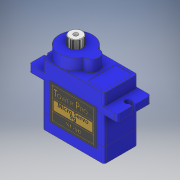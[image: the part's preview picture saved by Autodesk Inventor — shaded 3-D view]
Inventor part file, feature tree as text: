
AUTODESK INVENTOR PART (.ipt)
format: ipt  version: 2019 (Build 230136000, 136)  size: 1,554,432 bytes
history: native  units: in
note: dims shown in document units (in); Inventor stores cm internally (conversion verified against a paired STEP export)
features: other x13, plane x1, sketch x1
ambient origin geometry x8: Origin, YZ Plane, XZ Plane, XY Plane, X Axis, Y Axis, Z Axis, Center Point
bodies: Solid1 (feature_tree), Solid2 (feature_tree), Solid3 (feature_tree), Solid4 (feature_tree), Solid5 (feature_tree), Solid6 (feature_tree), Solid7 (feature_tree), Solid8 (feature_tree), Solid9 (feature_tree), Solid10 (feature_tree), Solid11 (feature_tree), Solid12 (feature_tree), Solid13 (feature_tree)
feature tree (15):
  plane  "Work Plane1"
  sketch  "Sketch1"  dims[d0=3.0in]
  other  "SG90 - Micro Servo 9g - Tower Pro.1-1-solid1"
  other  "SG90 - Micro Servo 9g - Tower Pro.1-1-solid2"
  other  "SG90 - Micro Servo 9g - Tower Pro.1-1-solid3"
  other  "SG90 - Micro Servo 9g - Tower Pro.1-1-solid4"
  other  "SG90 - Micro Servo 9g - Tower Pro.1-1-solid5"
  other  "SG90 - Micro Servo 9g - Tower Pro.1-1-solid6"
  other  "SG90 - Micro Servo 9g - Tower Pro.1-1-solid7"
  other  "SG90 - Micro Servo 9g - Tower Pro.1-1-solid8"
  other  "SG90 - Micro Servo 9g - Tower Pro.1-1-solid9"
  other  "SG90 - Micro Servo 9g - Tower Pro.1-1-solid10"
  other  "SG90 - Micro Servo 9g - Tower Pro.1-1-solid11"
  other  "SG90 - Micro Servo 9g - Tower Pro.1-1-solid12"
  other  "SG90 - Micro Servo 9g - Tower Pro.1-1-solid13"
